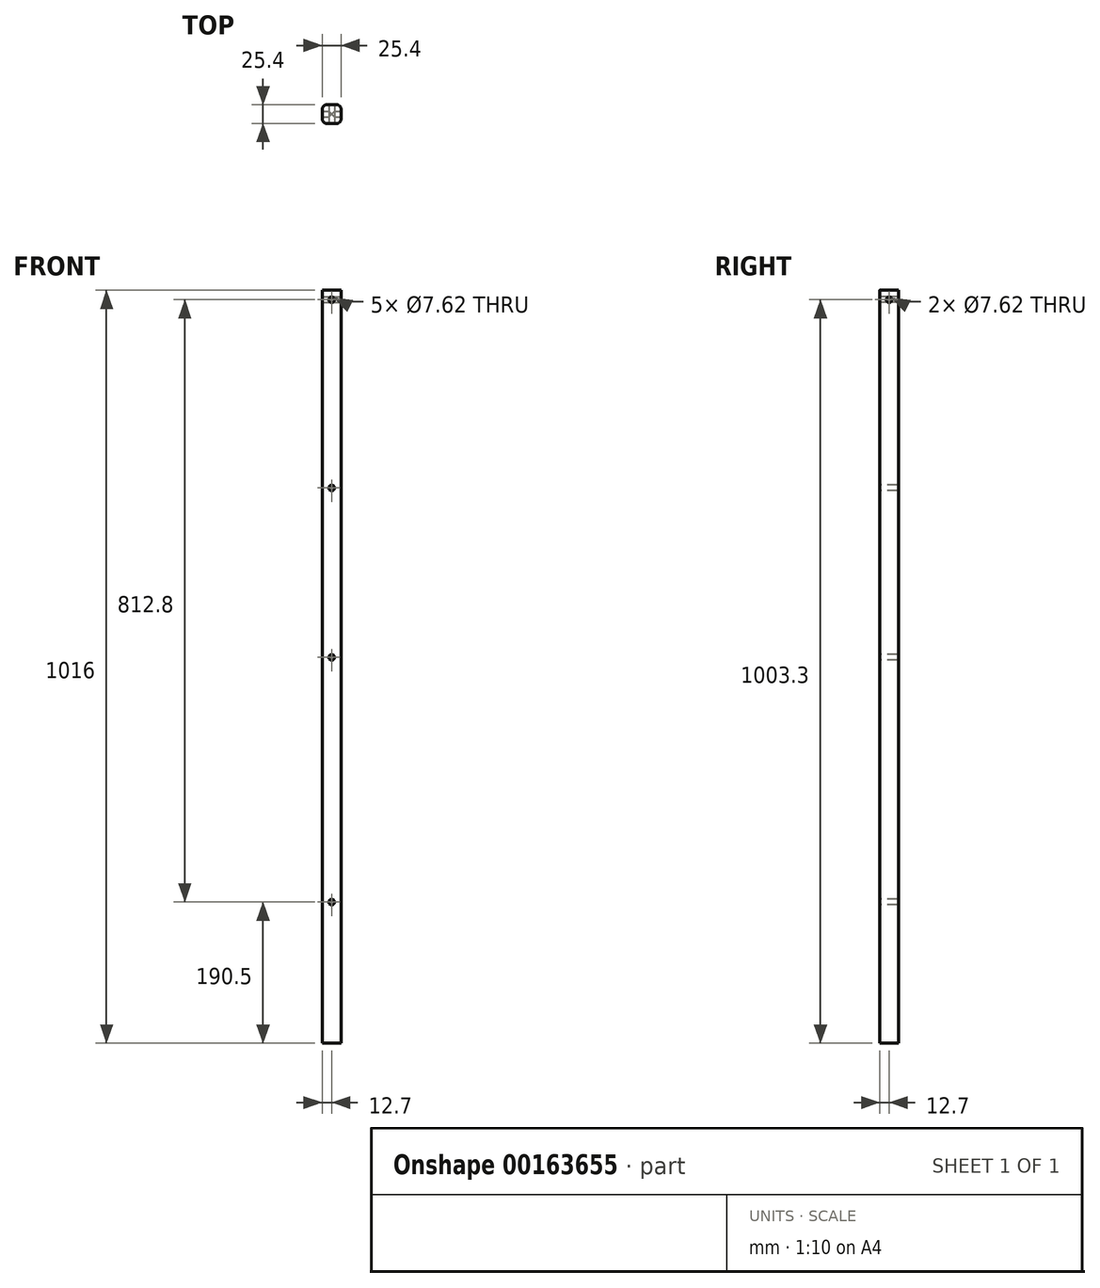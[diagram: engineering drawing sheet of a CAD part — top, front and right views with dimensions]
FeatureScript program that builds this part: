
annotation { "Feature Type Name" : "Feature", "Feature Type Description" : "" }
export const myFeature = defineFeature(function(context is Context, id is Id, definition is map)
    precondition{}
    {
        {
            var Q0;
            Q0=qCreatedBy(makeId("Top.planeOp"),FACE);
            var sketch = newSketch(context, id + "F0", { "sketchPlane" : qUnion([Q0])});
            skLineSegment(sketch, "E0.bottom", {"start": v(6.35, 12.7) * mm, "end": v(-6.35, 12.7) * mm});
            skLineSegment(sketch, "E0.top", {"start": v(6.35, -12.7) * mm, "end": v(-6.35, -12.7) * mm});
            skLineSegment(sketch, "E0.left", {"start": v(12.7, 6.35) * mm, "end": v(12.7, -6.35) * mm});
            skLineSegment(sketch, "E0.right", {"start": v(-12.7, 6.35) * mm, "end": v(-12.7, -6.35) * mm});
            skPoint(sketch, "E0.middle", {"position": v(0, 0) * mm});
            skPoint(sketch, "E1.visualSharp", {"position": v(-12.7, 12.7) * mm});
            skArc(sketch, "E1.filletArc", {"start": v(-6.35, 12.7) * mm, "mid": v(-10.84, 10.84) * mm, "end": v(-12.7, 6.35) * mm});
            skPoint(sketch, "E2.visualSharp", {"position": v(-12.7, -12.7) * mm});
            skArc(sketch, "E2.filletArc", {"start": v(-12.7, -6.35) * mm, "mid": v(-10.84, -10.84) * mm, "end": v(-6.35, -12.7) * mm});
            skPoint(sketch, "E3.visualSharp", {"position": v(12.7, -12.7) * mm});
            skArc(sketch, "E3.filletArc", {"start": v(6.35, -12.7) * mm, "mid": v(10.84, -10.84) * mm, "end": v(12.7, -6.35) * mm});
            skPoint(sketch, "E4.visualSharp", {"position": v(12.7, 12.7) * mm});
            skArc(sketch, "E4.filletArc", {"start": v(12.7, 6.35) * mm, "mid": v(10.84, 10.84) * mm, "end": v(6.35, 12.7) * mm});
            skSolve(sketch);
        }
        {
            var Q0;
            Q0=qSketchRegion(id+"F0",true);
            extrude(context, id + "F1", {"entities" : qUnion([Q0]), "depth" : 1016 * mm});
        }
        {
            var Q0;
            Q0=makeQuery(id+"F1.opExtrude","SWEPT_FACE",FACE,{"disambiguationData":[OSD([sQuery(id+"F0.wireOp",EDGE,"E0.top")])]});
            var sketch = newSketch(context, id + "F2", { "sketchPlane" : qUnion([Q0])});
            skLineSegment(sketch, "E5", {"start": v(0, 1016) * mm, "end": v(0, 1003.3) * mm});
            skPoint(sketch, "E5.endSnap0", {"position": v(0, 1016) * mm});
            skCircle(sketch, "E6", {"center": v(0, 1003.3) * mm, "radius": 3.81 * mm});
            skLineSegment(sketch, "E7", {"start": v(0, 1016) * mm, "end": v(0, 749.3) * mm, "construction": true});
            skLineSegment(sketch, "E8", {"start": v(0, 749.3) * mm, "end": v(0, 520.7) * mm, "construction": true});
            skCircle(sketch, "E9", {"center": v(0, 749.3) * mm, "radius": 3.81 * mm});
            skCircle(sketch, "E10", {"center": v(0, 520.7) * mm, "radius": 3.81 * mm});
            skLineSegment(sketch, "E11", {"start": v(0, 0) * mm, "end": v(0, 190.5) * mm, "construction": true});
            skCircle(sketch, "E12", {"center": v(0, 190.5) * mm, "radius": 3.81 * mm});
            skSolve(sketch);
        }
        {
            var Q0;
            Q0=makeQuery(id+"F2.imprint","IMPRINT",FACE,{"disambiguationData":[TD([[makeQuery(id+"F2.imprint","IMPRINT",EDGE,{"derivedFrom":sQuery(id+"F2.wireOp",EDGE,"E6")}),1.0]])]});
            extrude(context, id + "F3", {"entities" : qUnion([Q0]), "operationType" : NewBodyOperationType.REMOVE, "oppositeDirection" : true, "depth" : 25.4 * mm});
        }
        {
            var Q0;
            Q0=makeQuery(id+"F1.opExtrude","SWEPT_FACE",FACE,{"disambiguationData":[OSD([sQuery(id+"F0.wireOp",EDGE,"E0.left")])]});
            var sketch = newSketch(context, id + "F4", { "sketchPlane" : qUnion([Q0])});
            skPoint(sketch, "E13.endSnap0", {"position": v(0, 0) * mm});
            skLineSegment(sketch, "E14", {"start": v(0, 1016) * mm, "end": v(0, 1003.3) * mm});
            skPoint(sketch, "E14.endSnap0", {"position": v(0, 1016) * mm});
            skCircle(sketch, "E15", {"center": v(0, 1003.3) * mm, "radius": 3.81 * mm});
            skSolve(sketch);
        }
        {
            var Q0;
            Q0=makeQuery(id+"F4.imprint","IMPRINT",FACE,{"disambiguationData":[TD([[makeQuery(id+"F4.imprint","IMPRINT",EDGE,{"derivedFrom":sQuery(id+"F4.wireOp",EDGE,"E15")}),1.0]])]});
            var Q1;
            Q1=makeQuery(id+"F4.imprint","IMPRINT",FACE,{"disambiguationData":[TD([[makeQuery(id+"F4.imprint","IMPRINT",EDGE,{"derivedFrom":sQuery(id+"F4.wireOp",EDGE,"lmDfIelr-ZgLB-w0VR-bYfO-nWPvI039pRaW")}),1.0]])]});
            extrude(context, id + "F5", {"entities" : qUnion([Q0, Q1]), "operationType" : NewBodyOperationType.REMOVE, "oppositeDirection" : true, "depth" : 25.4 * mm});
        }
        {
            var Q0;
            Q0=makeQuery(id+"F2.imprint","IMPRINT",FACE,{"disambiguationData":[TD([[makeQuery(id+"F2.imprint","IMPRINT",EDGE,{"derivedFrom":sQuery(id+"F2.wireOp",EDGE,"E9")}),1.0]])]});
            var Q1;
            Q1=makeQuery(id+"F2.imprint","IMPRINT",FACE,{"disambiguationData":[TD([[makeQuery(id+"F2.imprint","IMPRINT",EDGE,{"derivedFrom":sQuery(id+"F2.wireOp",EDGE,"E10")}),1.0]])]});
            extrude(context, id + "F6", {"entities" : qUnion([Q0, Q1]), "operationType" : NewBodyOperationType.REMOVE, "oppositeDirection" : true, "depth" : 25.4 * mm, "offsetDistance" : 25.4 * mm});
        }
        {
            var Q0;
            Q0=makeQuery(id+"F2.imprint","IMPRINT",FACE,{"disambiguationData":[TD([[makeQuery(id+"F2.imprint","IMPRINT",EDGE,{"derivedFrom":sQuery(id+"F2.wireOp",EDGE,"E12")}),1.0]])]});
            extrude(context, id + "F7", {"entities" : qUnion([Q0]), "operationType" : NewBodyOperationType.REMOVE, "oppositeDirection" : true, "depth" : 25.4 * mm, "offsetDistance" : 25.4 * mm});
        }
    });
